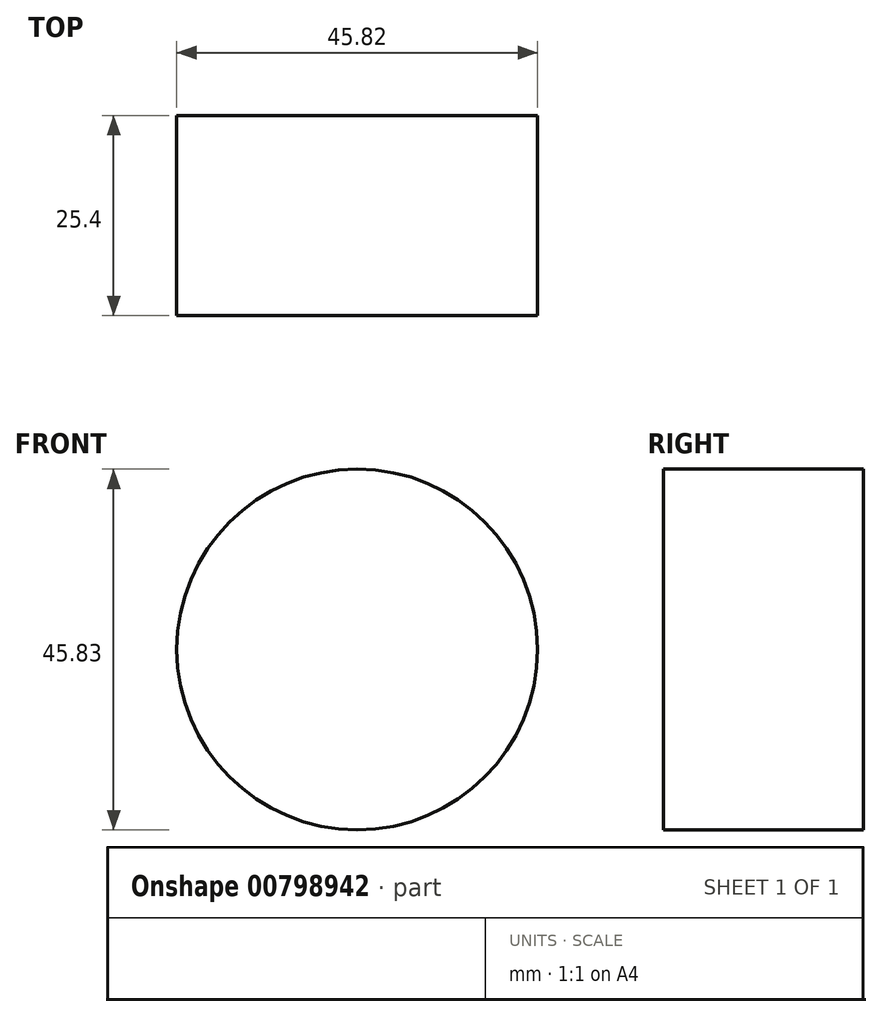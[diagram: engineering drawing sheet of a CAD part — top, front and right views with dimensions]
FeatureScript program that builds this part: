
annotation { "Feature Type Name" : "Feature", "Feature Type Description" : "" }
export const myFeature = defineFeature(function(context is Context, id is Id, definition is map)
    precondition{}
    {
        {
            var Q0;
            Q0=qCreatedBy(makeId("Front.planeOp"),FACE);
            var sketch = newSketch(context, id + "F0", { "sketchPlane" : qUnion([Q0])});
            skCircle(sketch, "E0", {"center": v(52.98, 19.2) * mm, "radius": 22.91 * mm});
            skSolve(sketch);
        }
        {
            var Q0;
            Q0 = qSketchRegion(id + "F0", true);
            extrude(context, id + "F1", {"entities" : qUnion([Q0]), "depth" : 25.4 * mm, "offsetDistance" : 25.4 * mm});
        }
    });
